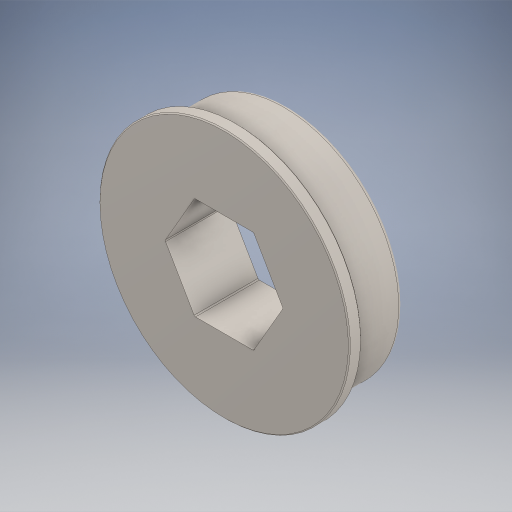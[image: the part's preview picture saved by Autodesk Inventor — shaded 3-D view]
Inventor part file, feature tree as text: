
AUTODESK INVENTOR PART (.ipt)
format: ipt  version: 2024.2 (Build 282272000, 272)  size: 314,880 bytes
history: native  units: in
note: dims shown in document units (in); Inventor stores cm internally (conversion verified against a paired STEP export)
features: fillet x1
ambient origin geometry x8: Origin, YZ Plane, XZ Plane, XY Plane, X Axis, Y Axis, Z Axis, Center Point
bodies: Solid1 (feature_tree)
feature tree (1):
  fillet  "Fillet2"  [1 undecoded]
note: 1 required parameter value undecoded (feature->parameter linkage not recoverable at this tier; creation-order binding heuristic only, values carry confidence <= 0.55)
